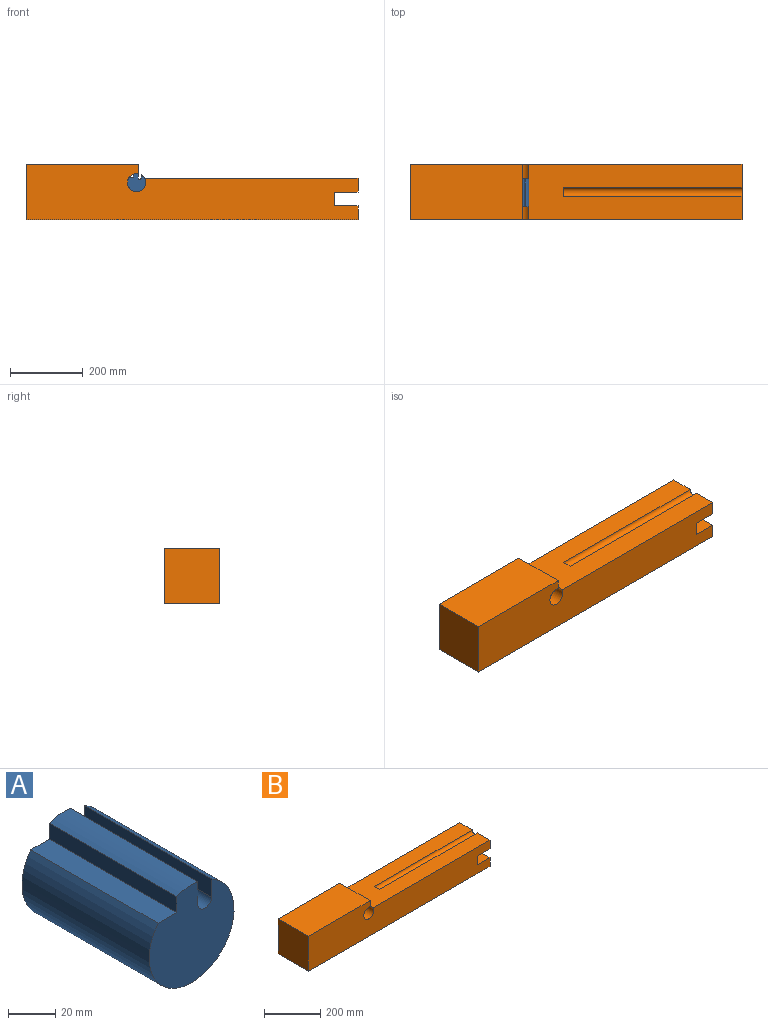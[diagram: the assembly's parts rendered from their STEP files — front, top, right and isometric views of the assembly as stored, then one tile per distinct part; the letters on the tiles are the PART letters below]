
ASSEMBLY  parts=2 mates=1
PART A: 9 faces, bbox 50.8x76.2x50.8 mm
  f0: cylinder r=25.4mm len=76.2mm, axis (0,1,0), area 990.1mm2, adj f1,f3,f5,f7
  f1: plane 50.8x50.8mm, normal (0,1,0), area 1855.6mm2, adj f0,f2,f4,f5,f6,f7,f8
  f2: cylinder r=25.4mm len=76.2mm, axis (0,1,0), area 9423.6mm2, adj f1,f3,f4,f6
  f3: plane 50.8x50.8mm, normal (0,-1,0), area 1855.6mm2, adj f0,f2,f4,f5,f6,f7,f8
  f4: plane 76.2x11.12mm, normal (0,0,1), area 847.6mm2, adj f1,f2,f3,f5
  f5: plane 76.2x8.26mm, normal (-1,0,0), area 629.1mm2, adj f0,f1,f3,f4
  f6: plane 76.2x9.43mm, normal (-1,0,0), area 718.3mm2, adj f1,f2,f3,f8
  f7: plane 76.2x12.25mm, normal (1,0,0), area 933.4mm2, adj f0,f1,f3,f8
  f8: cylinder r=4.24mm len=76.2mm, axis (0,-1,0), area 922.7mm2, adj f1,f3,f6,f7
PART B: 20 faces, bbox 914.4x152.4x152.4 mm
  f0: plane 152.4x38.1mm, normal (1,0,0), area 5553.1mm2, adj f1,f2,f8,f15,f18
  f1: plane 914.4x152.4mm, normal (0,-1,0), area 112043.7mm2, adj f0,f2,f3,f4,f5,f6,f7,f14
  f2: plane 587.6x152.4mm, normal (0,0,1), area 77034.6mm2, adj f0,f1,f4,f8,f15,f16
  f3: plane 311.15x152.4mm, normal (0,0,1), area 47419.3mm2, adj f1,f5,f8,f14
  f4: cylinder r=25.4mm len=152.4mm, axis (0,-1,0), area 17192.8mm2, adj f1,f2,f8,f10,f11,f12,f13,f14
  f5: plane 152.4x152.4mm, normal (-1,0,0), area 23225.8mm2, adj f1,f3,f6,f8
  f6: plane 914.4x152.4mm, normal (0,0,-1), area 132903mm2, adj f1,f5,f7,f8,f9,f10,f11,f12
  f7: plane 152.4x38.1mm, normal (1,0,0), area 5806.4mm2, adj f1,f6,f8,f17
  f8: plane 914.4x152.4mm, normal (0,1,0), area 112043.7mm2, adj f0,f2,f3,f4,f5,f6,f7,f14
  f9: plane 101.6x50.8mm, normal (-1,0,0), area 5161.3mm2, adj f6,f10,f12,f13
  f10: plane 127x101.6mm, normal (0,1,0), area 11889.8mm2, adj f4,f6,f9,f11,f13
  f11: plane 101.6x50.8mm, normal (1,0,0), area 5161.3mm2, adj f4,f6,f10,f12
  f12: plane 127x101.6mm, normal (0,-1,0), area 11889.8mm2, adj f4,f6,f9,f11,f13
  f13: plane 76.2x50.8mm, normal (0,0,-1), area 3871mm2, adj f4,f9,f10,f12
  f14: plane 152.4x26.21mm, normal (1,0,0), area 3993.9mm2, adj f1,f3,f4,f8
  f15: cylinder r=12.7mm len=492.76mm, axis (1,0,0), area 19660.3mm2, adj f0,f2,f16
  f16: plane 25.4x12.7mm, normal (1,0,0), area 253.4mm2, adj f2,f15
  f17: plane 152.4x63.5mm, normal (0,0,1), area 9677.4mm2, adj f1,f7,f8,f19
  f18: plane 152.4x63.5mm, normal (0,0,-1), area 9677.4mm2, adj f0,f1,f8,f19
  f19: plane 152.4x38.1mm, normal (1,0,0), area 5806.4mm2, adj f1,f8,f17,f18
PLACE A t=(-314.23,-82.17,-1.66)mm
PLACE B t=(-161.83,-41.95,-27.06)mm
MATE cylindrical A.f0 <-> B.f4  axis (0,1,0) through (-314.23,-120.27,-1.66)mm
